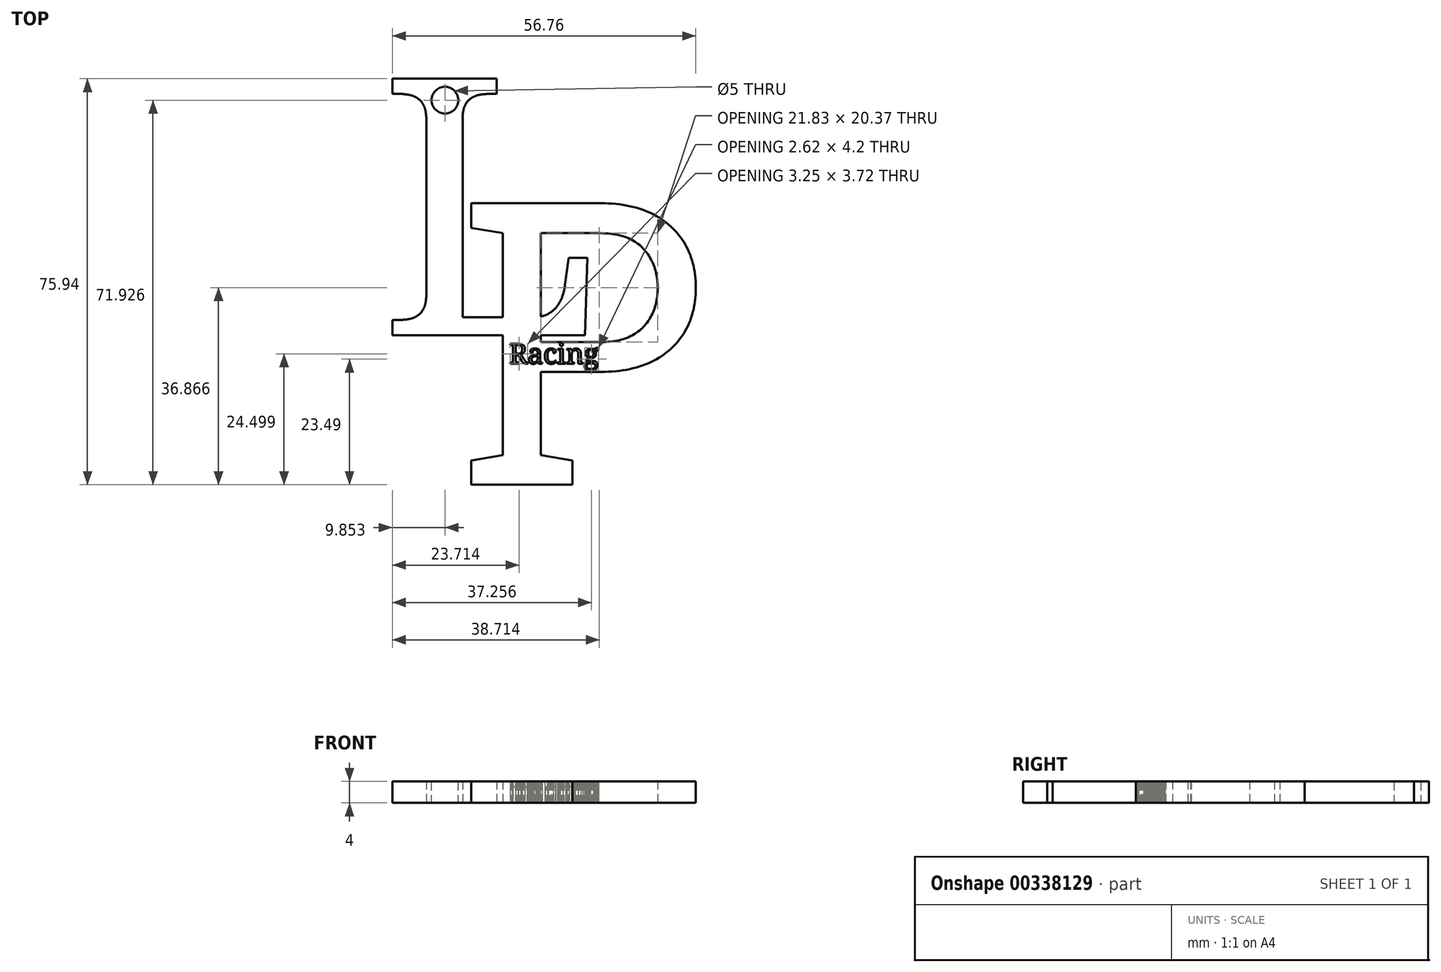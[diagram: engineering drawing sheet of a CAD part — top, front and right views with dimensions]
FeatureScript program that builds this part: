
annotation { "Feature Type Name" : "Feature", "Feature Type Description" : "" }
export const myFeature = defineFeature(function(context is Context, id is Id, definition is map)
    precondition{}
    {
        {
            var Q0;
            Q0=qCreatedBy(makeId("Top.planeOp"),FACE);
            var sketch = newSketch(context, id + "F0", { "sketchPlane" : qUnion([Q0])});
            skText(sketch, "E0", { "text": "L", "fontName": "NotoSerif-Regular.ttf"});
            skText(sketch, "E1", { "text": "P", "fontName": "RobotoSlab-Regular.ttf"});
            skText(sketch, "E2", { "text": "Racing", "fontName": "NotoSerif-Regular.ttf"});
            const initialGuessF0  = {"E0": [-0.08175, -0.00586, 1, 0, 0.04837], "E1": [-0.06698, -0.03384, 1, 0, 0.05332], "E2": [-0.0573, -0.0112, 1, 0, 0.00375]};
            skSetInitialGuess(sketch, initialGuessF0);
            skSolve(sketch);
        }
        {
            var Q0;
            Q0=makeQuery(id+"F0.imprint","IMPRINT",FACE,{"disambiguationData":[TD([[makeQuery(id+"F0.imprint","IMPRINT",EDGE,{"derivedFrom":sQuery(id+"F0.wireOp",EDGE,"E2.sketch_text.stroke-0")}),-1.0]])]});
            var Q1;
            Q1=makeQuery(id+"F0.imprint","IMPRINT",FACE,{"disambiguationData":[TD([[makeQuery(id+"F0.imprint","IMPRINT",EDGE,{"derivedFrom":sQuery(id+"F0.wireOp",EDGE,"E2.sketch_text.stroke-51")}),-1.0]])]});
            var Q2;
            Q2=makeQuery(id+"F0.imprint","IMPRINT",FACE,{"disambiguationData":[TD([[makeQuery(id+"F0.imprint","IMPRINT",EDGE,{"derivedFrom":sQuery(id+"F0.wireOp",EDGE,"E2.sketch_text.stroke-103")}),-1.0]])]});
            var Q3;
            Q3=makeQuery(id+"F0.imprint","IMPRINT",FACE,{"disambiguationData":[TD([[makeQuery(id+"F0.imprint","IMPRINT",EDGE,{"derivedFrom":sQuery(id+"F0.wireOp",EDGE,"E2.sketch_text.stroke-135")}),-1.0]])]});
            var Q4;
            Q4=makeQuery(id+"F0.imprint","IMPRINT",FACE,{"disambiguationData":[TD([[makeQuery(id+"F0.imprint","IMPRINT",EDGE,{"derivedFrom":sQuery(id+"F0.wireOp",EDGE,"E2.sketch_text.stroke-157")}),-1.0]])]});
            var Q5;
            Q5=makeQuery(id+"F0.imprint","IMPRINT",FACE,{"disambiguationData":[TD([[makeQuery(id+"F0.imprint","IMPRINT",EDGE,{"derivedFrom":sQuery(id+"F0.wireOp",EDGE,"E2.sketch_text.stroke-173")}),-1.0]])]});
            var Q6;
            Q6=makeQuery(id+"F0.imprint","IMPRINT",FACE,{"disambiguationData":[TD([[makeQuery(id+"F0.imprint","IMPRINT",EDGE,{"derivedFrom":sQuery(id+"F0.wireOp",EDGE,"E2.sketch_text.stroke-222")}),-1.0]])]});
            extrude(context, id + "F1", {"entities" : qUnion([Q0, Q1, Q2, Q3, Q4, Q5, Q6]), "depth" : 3 * mm});
        }
        {
            var Q0;
            Q0=makeQuery(id+"F0.imprint","IMPRINT",FACE,{"disambiguationData":[TD([[makeQuery(id+"F0.imprint","IMPRINT",EDGE,{"derivedFrom":sQuery(id+"F0.wireOp",EDGE,"E2.sketch_text.stroke-40")}),1.0]])]});
            var Q1;
            Q1=makeQuery(id+"F0.imprint","IMPRINT",FACE,{"disambiguationData":[TD([[makeQuery(id+"F0.imprint","IMPRINT",EDGE,{"derivedFrom":sQuery(id+"F0.wireOp",EDGE,"E2.sketch_text.stroke-51")}),1.0]])]});
            var Q2;
            Q2=makeQuery(id+"F0.imprint","IMPRINT",FACE,{"disambiguationData":[TD([[makeQuery(id+"F0.imprint","IMPRINT",EDGE,{"derivedFrom":sQuery(id+"F0.wireOp",EDGE,"E2.sketch_text.stroke-308")}),1.0]])]});
            var Q3;
            Q3=makeQuery(id+"F0.imprint","IMPRINT",FACE,{"disambiguationData":[TD([[makeQuery(id+"F0.imprint","IMPRINT",EDGE,{"derivedFrom":sQuery(id+"F0.wireOp",EDGE,"E2.sketch_text.stroke-291")}),1.0]])]});
            var Q4;
            Q4=makeQuery(id+"F0.imprint","IMPRINT",FACE,{"disambiguationData":[TD([[makeQuery(id+"F0.imprint","IMPRINT",EDGE,{"derivedFrom":sQuery(id+"F0.wireOp",EDGE,"E1.sketch_text.stroke-0")}),-1.0]])]});
            var Q5;
            {var subQ5=sQuery(id+"F0.wireOp",EDGE,"E0.sketch_text.stroke-23");Q5=makeQuery(id+"F0.imprint","IMPRINT",FACE,{"disambiguationData":[TD([[makeQuery(id+"F0.imprint","IMPRINT",EDGE,{"derivedFrom":subQ5}),-1.0]])]});}
            var Q6;
            {var subQ4=sQuery(id+"F0.wireOp",EDGE,"E0.sketch_text.stroke-0");Q6=makeQuery(id+"F0.imprint","IMPRINT",FACE,{"disambiguationData":[TD([[makeQuery(id+"F0.imprint","IMPRINT",EDGE,{"derivedFrom":subQ4}),-1.0]])]});}
            var Q7;
            {var subQ1=sQuery(id+"F0.wireOp",EDGE,"E0.sketch_text.stroke-21");var subQ5=sQuery(id+"F0.wireOp",EDGE,"E0.sketch_text.stroke-22");var subQ6=makeQuery(id+"F0.imprint","INTERSECT",VERTEX,{"derivedFrom":[subQ1,subQ5]});Q7=makeQuery(id+"F0.imprint","IMPRINT",FACE,{"disambiguationData":[TD([[makeQuery(id+"F0.imprint","IMPRINT",EDGE,{"disambiguationData":[TD([[subQ6,1.0]])],"derivedFrom":subQ1}),-1.0]])]});}
            extrude(context, id + "F2", {"entities" : qUnion([Q0, Q1, Q2, Q3, Q4, Q5, Q6, Q7]), "depth" : 4 * mm});
        }
        {
            var Q0;
            Q0=makeQuery(id+"F2.opExtrude","CAP_FACE",FACE,{"disambiguationData":[OSD([sQuery(id+"F0.wireOp",EDGE,"E0.sketch_text.stroke-0"),sQuery(id+"F0.wireOp",EDGE,"E0.sketch_text.stroke-1"),sQuery(id+"F0.wireOp",EDGE,"E0.sketch_text.stroke-2"),sQuery(id+"F0.wireOp",EDGE,"E0.sketch_text.stroke-3"),sQuery(id+"F0.wireOp",EDGE,"E0.sketch_text.stroke-4"),sQuery(id+"F0.wireOp",EDGE,"E0.sketch_text.stroke-5"),sQuery(id+"F0.wireOp",EDGE,"E0.sketch_text.stroke-6"),sQuery(id+"F0.wireOp",EDGE,"E0.sketch_text.stroke-7"),sQuery(id+"F0.wireOp",EDGE,"E0.sketch_text.stroke-8"),sQuery(id+"F0.wireOp",EDGE,"E0.sketch_text.stroke-9"),sQuery(id+"F0.wireOp",EDGE,"E0.sketch_text.stroke-10"),sQuery(id+"F0.wireOp",EDGE,"E0.sketch_text.stroke-11"),sQuery(id+"F0.wireOp",EDGE,"E0.sketch_text.stroke-12"),sQuery(id+"F0.wireOp",EDGE,"E0.sketch_text.stroke-13"),sQuery(id+"F0.wireOp",EDGE,"E0.sketch_text.stroke-14"),sQuery(id+"F0.wireOp",EDGE,"E0.sketch_text.stroke-15"),sQuery(id+"F0.wireOp",EDGE,"E0.sketch_text.stroke-16"),sQuery(id+"F0.wireOp",EDGE,"E0.sketch_text.stroke-17"),sQuery(id+"F0.wireOp",EDGE,"E0.sketch_text.stroke-18"),sQuery(id+"F0.wireOp",EDGE,"E0.sketch_text.stroke-19"),sQuery(id+"F0.wireOp",EDGE,"E0.sketch_text.stroke-20"),sQuery(id+"F0.wireOp",EDGE,"E0.sketch_text.stroke-21"),sQuery(id+"F0.wireOp",EDGE,"E0.sketch_text.stroke-22"),sQuery(id+"F0.wireOp",EDGE,"E0.sketch_text.stroke-23"),sQuery(id+"F0.wireOp",EDGE,"E0.sketch_text.stroke-24"),sQuery(id+"F0.wireOp",EDGE,"E0.sketch_text.stroke-25"),sQuery(id+"F0.wireOp",EDGE,"E0.sketch_text.stroke-26"),sQuery(id+"F0.wireOp",EDGE,"E0.sketch_text.stroke-27"),sQuery(id+"F0.wireOp",EDGE,"E0.sketch_text.stroke-28"),sQuery(id+"F0.wireOp",EDGE,"E0.sketch_text.stroke-29"),sQuery(id+"F0.wireOp",EDGE,"E1.sketch_text.stroke-0"),sQuery(id+"F0.wireOp",EDGE,"E1.sketch_text.stroke-1"),sQuery(id+"F0.wireOp",EDGE,"E1.sketch_text.stroke-2"),sQuery(id+"F0.wireOp",EDGE,"E1.sketch_text.stroke-3"),sQuery(id+"F0.wireOp",EDGE,"E1.sketch_text.stroke-4"),sQuery(id+"F0.wireOp",EDGE,"E1.sketch_text.stroke-5"),sQuery(id+"F0.wireOp",EDGE,"E1.sketch_text.stroke-6"),sQuery(id+"F0.wireOp",EDGE,"E1.sketch_text.stroke-7"),sQuery(id+"F0.wireOp",EDGE,"E1.sketch_text.stroke-8"),sQuery(id+"F0.wireOp",EDGE,"E1.sketch_text.stroke-9"),sQuery(id+"F0.wireOp",EDGE,"E1.sketch_text.stroke-10"),sQuery(id+"F0.wireOp",EDGE,"E1.sketch_text.stroke-11"),sQuery(id+"F0.wireOp",EDGE,"E1.sketch_text.stroke-12"),sQuery(id+"F0.wireOp",EDGE,"E1.sketch_text.stroke-13"),sQuery(id+"F0.wireOp",EDGE,"E1.sketch_text.stroke-14"),sQuery(id+"F0.wireOp",EDGE,"E1.sketch_text.stroke-15"),sQuery(id+"F0.wireOp",EDGE,"E1.sketch_text.stroke-16"),sQuery(id+"F0.wireOp",EDGE,"E1.sketch_text.stroke-17"),sQuery(id+"F0.wireOp",EDGE,"E1.sketch_text.stroke-18"),sQuery(id+"F0.wireOp",EDGE,"E1.sketch_text.stroke-19"),sQuery(id+"F0.wireOp",EDGE,"E1.sketch_text.stroke-20"),sQuery(id+"F0.wireOp",EDGE,"E1.sketch_text.stroke-21"),sQuery(id+"F0.wireOp",EDGE,"E1.sketch_text.stroke-22"),sQuery(id+"F0.wireOp",EDGE,"E2.sketch_text.stroke-0"),sQuery(id+"F0.wireOp",EDGE,"E2.sketch_text.stroke-1"),sQuery(id+"F0.wireOp",EDGE,"E2.sketch_text.stroke-2"),sQuery(id+"F0.wireOp",EDGE,"E2.sketch_text.stroke-3"),sQuery(id+"F0.wireOp",EDGE,"E2.sketch_text.stroke-4"),sQuery(id+"F0.wireOp",EDGE,"E2.sketch_text.stroke-5"),sQuery(id+"F0.wireOp",EDGE,"E2.sketch_text.stroke-6"),sQuery(id+"F0.wireOp",EDGE,"E2.sketch_text.stroke-7"),sQuery(id+"F0.wireOp",EDGE,"E2.sketch_text.stroke-8"),sQuery(id+"F0.wireOp",EDGE,"E2.sketch_text.stroke-9"),sQuery(id+"F0.wireOp",EDGE,"E2.sketch_text.stroke-10"),sQuery(id+"F0.wireOp",EDGE,"E2.sketch_text.stroke-11"),sQuery(id+"F0.wireOp",EDGE,"E2.sketch_text.stroke-12"),sQuery(id+"F0.wireOp",EDGE,"E2.sketch_text.stroke-13"),sQuery(id+"F0.wireOp",EDGE,"E2.sketch_text.stroke-14"),sQuery(id+"F0.wireOp",EDGE,"E2.sketch_text.stroke-15"),sQuery(id+"F0.wireOp",EDGE,"E2.sketch_text.stroke-16"),sQuery(id+"F0.wireOp",EDGE,"E2.sketch_text.stroke-17"),sQuery(id+"F0.wireOp",EDGE,"E2.sketch_text.stroke-18"),sQuery(id+"F0.wireOp",EDGE,"E2.sketch_text.stroke-19"),sQuery(id+"F0.wireOp",EDGE,"E2.sketch_text.stroke-20"),sQuery(id+"F0.wireOp",EDGE,"E2.sketch_text.stroke-21"),sQuery(id+"F0.wireOp",EDGE,"E2.sketch_text.stroke-22"),sQuery(id+"F0.wireOp",EDGE,"E2.sketch_text.stroke-23"),sQuery(id+"F0.wireOp",EDGE,"E2.sketch_text.stroke-24"),sQuery(id+"F0.wireOp",EDGE,"E2.sketch_text.stroke-25"),sQuery(id+"F0.wireOp",EDGE,"E2.sketch_text.stroke-26"),sQuery(id+"F0.wireOp",EDGE,"E2.sketch_text.stroke-27"),sQuery(id+"F0.wireOp",EDGE,"E2.sketch_text.stroke-28"),sQuery(id+"F0.wireOp",EDGE,"E2.sketch_text.stroke-29"),sQuery(id+"F0.wireOp",EDGE,"E2.sketch_text.stroke-30"),sQuery(id+"F0.wireOp",EDGE,"E2.sketch_text.stroke-31"),sQuery(id+"F0.wireOp",EDGE,"E2.sketch_text.stroke-32"),sQuery(id+"F0.wireOp",EDGE,"E2.sketch_text.stroke-33"),sQuery(id+"F0.wireOp",EDGE,"E2.sketch_text.stroke-34"),sQuery(id+"F0.wireOp",EDGE,"E2.sketch_text.stroke-35"),sQuery(id+"F0.wireOp",EDGE,"E2.sketch_text.stroke-36"),sQuery(id+"F0.wireOp",EDGE,"E2.sketch_text.stroke-37"),sQuery(id+"F0.wireOp",EDGE,"E2.sketch_text.stroke-38"),sQuery(id+"F0.wireOp",EDGE,"E2.sketch_text.stroke-39"),sQuery(id+"F0.wireOp",EDGE,"E2.sketch_text.stroke-63"),sQuery(id+"F0.wireOp",EDGE,"E2.sketch_text.stroke-64"),sQuery(id+"F0.wireOp",EDGE,"E2.sketch_text.stroke-65"),sQuery(id+"F0.wireOp",EDGE,"E2.sketch_text.stroke-66"),sQuery(id+"F0.wireOp",EDGE,"E2.sketch_text.stroke-67"),sQuery(id+"F0.wireOp",EDGE,"E2.sketch_text.stroke-68"),sQuery(id+"F0.wireOp",EDGE,"E2.sketch_text.stroke-69"),sQuery(id+"F0.wireOp",EDGE,"E2.sketch_text.stroke-70"),sQuery(id+"F0.wireOp",EDGE,"E2.sketch_text.stroke-71"),sQuery(id+"F0.wireOp",EDGE,"E2.sketch_text.stroke-72"),sQuery(id+"F0.wireOp",EDGE,"E2.sketch_text.stroke-73"),sQuery(id+"F0.wireOp",EDGE,"E2.sketch_text.stroke-74"),sQuery(id+"F0.wireOp",EDGE,"E2.sketch_text.stroke-75"),sQuery(id+"F0.wireOp",EDGE,"E2.sketch_text.stroke-76"),sQuery(id+"F0.wireOp",EDGE,"E2.sketch_text.stroke-77"),sQuery(id+"F0.wireOp",EDGE,"E2.sketch_text.stroke-78"),sQuery(id+"F0.wireOp",EDGE,"E2.sketch_text.stroke-79"),sQuery(id+"F0.wireOp",EDGE,"E2.sketch_text.stroke-80"),sQuery(id+"F0.wireOp",EDGE,"E2.sketch_text.stroke-81"),sQuery(id+"F0.wireOp",EDGE,"E2.sketch_text.stroke-82"),sQuery(id+"F0.wireOp",EDGE,"E2.sketch_text.stroke-83"),sQuery(id+"F0.wireOp",EDGE,"E2.sketch_text.stroke-84"),sQuery(id+"F0.wireOp",EDGE,"E2.sketch_text.stroke-85"),sQuery(id+"F0.wireOp",EDGE,"E2.sketch_text.stroke-86"),sQuery(id+"F0.wireOp",EDGE,"E2.sketch_text.stroke-87"),sQuery(id+"F0.wireOp",EDGE,"E2.sketch_text.stroke-88"),sQuery(id+"F0.wireOp",EDGE,"E2.sketch_text.stroke-89"),sQuery(id+"F0.wireOp",EDGE,"E2.sketch_text.stroke-90"),sQuery(id+"F0.wireOp",EDGE,"E2.sketch_text.stroke-91"),sQuery(id+"F0.wireOp",EDGE,"E2.sketch_text.stroke-92"),sQuery(id+"F0.wireOp",EDGE,"E2.sketch_text.stroke-93"),sQuery(id+"F0.wireOp",EDGE,"E2.sketch_text.stroke-94"),sQuery(id+"F0.wireOp",EDGE,"E2.sketch_text.stroke-95"),sQuery(id+"F0.wireOp",EDGE,"E2.sketch_text.stroke-96"),sQuery(id+"F0.wireOp",EDGE,"E2.sketch_text.stroke-97"),sQuery(id+"F0.wireOp",EDGE,"E2.sketch_text.stroke-98"),sQuery(id+"F0.wireOp",EDGE,"E2.sketch_text.stroke-99"),sQuery(id+"F0.wireOp",EDGE,"E2.sketch_text.stroke-100"),sQuery(id+"F0.wireOp",EDGE,"E2.sketch_text.stroke-101"),sQuery(id+"F0.wireOp",EDGE,"E2.sketch_text.stroke-102"),sQuery(id+"F0.wireOp",EDGE,"E2.sketch_text.stroke-103"),sQuery(id+"F0.wireOp",EDGE,"E2.sketch_text.stroke-104"),sQuery(id+"F0.wireOp",EDGE,"E2.sketch_text.stroke-105"),sQuery(id+"F0.wireOp",EDGE,"E2.sketch_text.stroke-106"),sQuery(id+"F0.wireOp",EDGE,"E2.sketch_text.stroke-107"),sQuery(id+"F0.wireOp",EDGE,"E2.sketch_text.stroke-108"),sQuery(id+"F0.wireOp",EDGE,"E2.sketch_text.stroke-109"),sQuery(id+"F0.wireOp",EDGE,"E2.sketch_text.stroke-110"),sQuery(id+"F0.wireOp",EDGE,"E2.sketch_text.stroke-111"),sQuery(id+"F0.wireOp",EDGE,"E2.sketch_text.stroke-112"),sQuery(id+"F0.wireOp",EDGE,"E2.sketch_text.stroke-113"),sQuery(id+"F0.wireOp",EDGE,"E2.sketch_text.stroke-114"),sQuery(id+"F0.wireOp",EDGE,"E2.sketch_text.stroke-115"),sQuery(id+"F0.wireOp",EDGE,"E2.sketch_text.stroke-116"),sQuery(id+"F0.wireOp",EDGE,"E2.sketch_text.stroke-117"),sQuery(id+"F0.wireOp",EDGE,"E2.sketch_text.stroke-118"),sQuery(id+"F0.wireOp",EDGE,"E2.sketch_text.stroke-119"),sQuery(id+"F0.wireOp",EDGE,"E2.sketch_text.stroke-120"),sQuery(id+"F0.wireOp",EDGE,"E2.sketch_text.stroke-121"),sQuery(id+"F0.wireOp",EDGE,"E2.sketch_text.stroke-122"),sQuery(id+"F0.wireOp",EDGE,"E2.sketch_text.stroke-123"),sQuery(id+"F0.wireOp",EDGE,"E2.sketch_text.stroke-124"),sQuery(id+"F0.wireOp",EDGE,"E2.sketch_text.stroke-125"),sQuery(id+"F0.wireOp",EDGE,"E2.sketch_text.stroke-126"),sQuery(id+"F0.wireOp",EDGE,"E2.sketch_text.stroke-127"),sQuery(id+"F0.wireOp",EDGE,"E2.sketch_text.stroke-128"),sQuery(id+"F0.wireOp",EDGE,"E2.sketch_text.stroke-129"),sQuery(id+"F0.wireOp",EDGE,"E2.sketch_text.stroke-130"),sQuery(id+"F0.wireOp",EDGE,"E2.sketch_text.stroke-131"),sQuery(id+"F0.wireOp",EDGE,"E2.sketch_text.stroke-132"),sQuery(id+"F0.wireOp",EDGE,"E2.sketch_text.stroke-133"),sQuery(id+"F0.wireOp",EDGE,"E2.sketch_text.stroke-134"),sQuery(id+"F0.wireOp",EDGE,"E2.sketch_text.stroke-135"),sQuery(id+"F0.wireOp",EDGE,"E2.sketch_text.stroke-136"),sQuery(id+"F0.wireOp",EDGE,"E2.sketch_text.stroke-137"),sQuery(id+"F0.wireOp",EDGE,"E2.sketch_text.stroke-138"),sQuery(id+"F0.wireOp",EDGE,"E2.sketch_text.stroke-139"),sQuery(id+"F0.wireOp",EDGE,"E2.sketch_text.stroke-140"),sQuery(id+"F0.wireOp",EDGE,"E2.sketch_text.stroke-141"),sQuery(id+"F0.wireOp",EDGE,"E2.sketch_text.stroke-142"),sQuery(id+"F0.wireOp",EDGE,"E2.sketch_text.stroke-143"),sQuery(id+"F0.wireOp",EDGE,"E2.sketch_text.stroke-144"),sQuery(id+"F0.wireOp",EDGE,"E2.sketch_text.stroke-145"),sQuery(id+"F0.wireOp",EDGE,"E2.sketch_text.stroke-146"),sQuery(id+"F0.wireOp",EDGE,"E2.sketch_text.stroke-147"),sQuery(id+"F0.wireOp",EDGE,"E2.sketch_text.stroke-148"),sQuery(id+"F0.wireOp",EDGE,"E2.sketch_text.stroke-149"),sQuery(id+"F0.wireOp",EDGE,"E2.sketch_text.stroke-150"),sQuery(id+"F0.wireOp",EDGE,"E2.sketch_text.stroke-151"),sQuery(id+"F0.wireOp",EDGE,"E2.sketch_text.stroke-152"),sQuery(id+"F0.wireOp",EDGE,"E2.sketch_text.stroke-153"),sQuery(id+"F0.wireOp",EDGE,"E2.sketch_text.stroke-154"),sQuery(id+"F0.wireOp",EDGE,"E2.sketch_text.stroke-155"),sQuery(id+"F0.wireOp",EDGE,"E2.sketch_text.stroke-156"),sQuery(id+"F0.wireOp",EDGE,"E2.sketch_text.stroke-157"),sQuery(id+"F0.wireOp",EDGE,"E2.sketch_text.stroke-158"),sQuery(id+"F0.wireOp",EDGE,"E2.sketch_text.stroke-159"),sQuery(id+"F0.wireOp",EDGE,"E2.sketch_text.stroke-160"),sQuery(id+"F0.wireOp",EDGE,"E2.sketch_text.stroke-161"),sQuery(id+"F0.wireOp",EDGE,"E2.sketch_text.stroke-162"),sQuery(id+"F0.wireOp",EDGE,"E2.sketch_text.stroke-163"),sQuery(id+"F0.wireOp",EDGE,"E2.sketch_text.stroke-164"),sQuery(id+"F0.wireOp",EDGE,"E2.sketch_text.stroke-165"),sQuery(id+"F0.wireOp",EDGE,"E2.sketch_text.stroke-166"),sQuery(id+"F0.wireOp",EDGE,"E2.sketch_text.stroke-167"),sQuery(id+"F0.wireOp",EDGE,"E2.sketch_text.stroke-168"),sQuery(id+"F0.wireOp",EDGE,"E2.sketch_text.stroke-169"),sQuery(id+"F0.wireOp",EDGE,"E2.sketch_text.stroke-170"),sQuery(id+"F0.wireOp",EDGE,"E2.sketch_text.stroke-171"),sQuery(id+"F0.wireOp",EDGE,"E2.sketch_text.stroke-172"),sQuery(id+"F0.wireOp",EDGE,"E2.sketch_text.stroke-173"),sQuery(id+"F0.wireOp",EDGE,"E2.sketch_text.stroke-174"),sQuery(id+"F0.wireOp",EDGE,"E2.sketch_text.stroke-175"),sQuery(id+"F0.wireOp",EDGE,"E2.sketch_text.stroke-176"),sQuery(id+"F0.wireOp",EDGE,"E2.sketch_text.stroke-177"),sQuery(id+"F0.wireOp",EDGE,"E2.sketch_text.stroke-178"),sQuery(id+"F0.wireOp",EDGE,"E2.sketch_text.stroke-179"),sQuery(id+"F0.wireOp",EDGE,"E2.sketch_text.stroke-180"),sQuery(id+"F0.wireOp",EDGE,"E2.sketch_text.stroke-181"),sQuery(id+"F0.wireOp",EDGE,"E2.sketch_text.stroke-182"),sQuery(id+"F0.wireOp",EDGE,"E2.sketch_text.stroke-183"),sQuery(id+"F0.wireOp",EDGE,"E2.sketch_text.stroke-184"),sQuery(id+"F0.wireOp",EDGE,"E2.sketch_text.stroke-185"),sQuery(id+"F0.wireOp",EDGE,"E2.sketch_text.stroke-186"),sQuery(id+"F0.wireOp",EDGE,"E2.sketch_text.stroke-187"),sQuery(id+"F0.wireOp",EDGE,"E2.sketch_text.stroke-188"),sQuery(id+"F0.wireOp",EDGE,"E2.sketch_text.stroke-189"),sQuery(id+"F0.wireOp",EDGE,"E2.sketch_text.stroke-190"),sQuery(id+"F0.wireOp",EDGE,"E2.sketch_text.stroke-191"),sQuery(id+"F0.wireOp",EDGE,"E2.sketch_text.stroke-192"),sQuery(id+"F0.wireOp",EDGE,"E2.sketch_text.stroke-193"),sQuery(id+"F0.wireOp",EDGE,"E2.sketch_text.stroke-194"),sQuery(id+"F0.wireOp",EDGE,"E2.sketch_text.stroke-195"),sQuery(id+"F0.wireOp",EDGE,"E2.sketch_text.stroke-196"),sQuery(id+"F0.wireOp",EDGE,"E2.sketch_text.stroke-197"),sQuery(id+"F0.wireOp",EDGE,"E2.sketch_text.stroke-198"),sQuery(id+"F0.wireOp",EDGE,"E2.sketch_text.stroke-199"),sQuery(id+"F0.wireOp",EDGE,"E2.sketch_text.stroke-200"),sQuery(id+"F0.wireOp",EDGE,"E2.sketch_text.stroke-201"),sQuery(id+"F0.wireOp",EDGE,"E2.sketch_text.stroke-202"),sQuery(id+"F0.wireOp",EDGE,"E2.sketch_text.stroke-203"),sQuery(id+"F0.wireOp",EDGE,"E2.sketch_text.stroke-204"),sQuery(id+"F0.wireOp",EDGE,"E2.sketch_text.stroke-205"),sQuery(id+"F0.wireOp",EDGE,"E2.sketch_text.stroke-206"),sQuery(id+"F0.wireOp",EDGE,"E2.sketch_text.stroke-207"),sQuery(id+"F0.wireOp",EDGE,"E2.sketch_text.stroke-208"),sQuery(id+"F0.wireOp",EDGE,"E2.sketch_text.stroke-209"),sQuery(id+"F0.wireOp",EDGE,"E2.sketch_text.stroke-210"),sQuery(id+"F0.wireOp",EDGE,"E2.sketch_text.stroke-211"),sQuery(id+"F0.wireOp",EDGE,"E2.sketch_text.stroke-212"),sQuery(id+"F0.wireOp",EDGE,"E2.sketch_text.stroke-213"),sQuery(id+"F0.wireOp",EDGE,"E2.sketch_text.stroke-214"),sQuery(id+"F0.wireOp",EDGE,"E2.sketch_text.stroke-215"),sQuery(id+"F0.wireOp",EDGE,"E2.sketch_text.stroke-216"),sQuery(id+"F0.wireOp",EDGE,"E2.sketch_text.stroke-217"),sQuery(id+"F0.wireOp",EDGE,"E2.sketch_text.stroke-218"),sQuery(id+"F0.wireOp",EDGE,"E2.sketch_text.stroke-219"),sQuery(id+"F0.wireOp",EDGE,"E2.sketch_text.stroke-220"),sQuery(id+"F0.wireOp",EDGE,"E2.sketch_text.stroke-221"),sQuery(id+"F0.wireOp",EDGE,"E2.sketch_text.stroke-222"),sQuery(id+"F0.wireOp",EDGE,"E2.sketch_text.stroke-223"),sQuery(id+"F0.wireOp",EDGE,"E2.sketch_text.stroke-224"),sQuery(id+"F0.wireOp",EDGE,"E2.sketch_text.stroke-225"),sQuery(id+"F0.wireOp",EDGE,"E2.sketch_text.stroke-226"),sQuery(id+"F0.wireOp",EDGE,"E2.sketch_text.stroke-227"),sQuery(id+"F0.wireOp",EDGE,"E2.sketch_text.stroke-228"),sQuery(id+"F0.wireOp",EDGE,"E2.sketch_text.stroke-229"),sQuery(id+"F0.wireOp",EDGE,"E2.sketch_text.stroke-230"),sQuery(id+"F0.wireOp",EDGE,"E2.sketch_text.stroke-231"),sQuery(id+"F0.wireOp",EDGE,"E2.sketch_text.stroke-232"),sQuery(id+"F0.wireOp",EDGE,"E2.sketch_text.stroke-233"),sQuery(id+"F0.wireOp",EDGE,"E2.sketch_text.stroke-234"),sQuery(id+"F0.wireOp",EDGE,"E2.sketch_text.stroke-235"),sQuery(id+"F0.wireOp",EDGE,"E2.sketch_text.stroke-236"),sQuery(id+"F0.wireOp",EDGE,"E2.sketch_text.stroke-237"),sQuery(id+"F0.wireOp",EDGE,"E2.sketch_text.stroke-238"),sQuery(id+"F0.wireOp",EDGE,"E2.sketch_text.stroke-239"),sQuery(id+"F0.wireOp",EDGE,"E2.sketch_text.stroke-240"),sQuery(id+"F0.wireOp",EDGE,"E2.sketch_text.stroke-241"),sQuery(id+"F0.wireOp",EDGE,"E2.sketch_text.stroke-242"),sQuery(id+"F0.wireOp",EDGE,"E2.sketch_text.stroke-243"),sQuery(id+"F0.wireOp",EDGE,"E2.sketch_text.stroke-244"),sQuery(id+"F0.wireOp",EDGE,"E2.sketch_text.stroke-245"),sQuery(id+"F0.wireOp",EDGE,"E2.sketch_text.stroke-246"),sQuery(id+"F0.wireOp",EDGE,"E2.sketch_text.stroke-247"),sQuery(id+"F0.wireOp",EDGE,"E2.sketch_text.stroke-248"),sQuery(id+"F0.wireOp",EDGE,"E2.sketch_text.stroke-249"),sQuery(id+"F0.wireOp",EDGE,"E2.sketch_text.stroke-250"),sQuery(id+"F0.wireOp",EDGE,"E2.sketch_text.stroke-251"),sQuery(id+"F0.wireOp",EDGE,"E2.sketch_text.stroke-252"),sQuery(id+"F0.wireOp",EDGE,"E2.sketch_text.stroke-253"),sQuery(id+"F0.wireOp",EDGE,"E2.sketch_text.stroke-254"),sQuery(id+"F0.wireOp",EDGE,"E2.sketch_text.stroke-255"),sQuery(id+"F0.wireOp",EDGE,"E2.sketch_text.stroke-256"),sQuery(id+"F0.wireOp",EDGE,"E2.sketch_text.stroke-257"),sQuery(id+"F0.wireOp",EDGE,"E2.sketch_text.stroke-258"),sQuery(id+"F0.wireOp",EDGE,"E2.sketch_text.stroke-259"),sQuery(id+"F0.wireOp",EDGE,"E2.sketch_text.stroke-260"),sQuery(id+"F0.wireOp",EDGE,"E2.sketch_text.stroke-261"),sQuery(id+"F0.wireOp",EDGE,"E2.sketch_text.stroke-262"),sQuery(id+"F0.wireOp",EDGE,"E2.sketch_text.stroke-263"),sQuery(id+"F0.wireOp",EDGE,"E2.sketch_text.stroke-264"),sQuery(id+"F0.wireOp",EDGE,"E2.sketch_text.stroke-265"),sQuery(id+"F0.wireOp",EDGE,"E2.sketch_text.stroke-266"),sQuery(id+"F0.wireOp",EDGE,"E2.sketch_text.stroke-267"),sQuery(id+"F0.wireOp",EDGE,"E2.sketch_text.stroke-268"),sQuery(id+"F0.wireOp",EDGE,"E2.sketch_text.stroke-269"),sQuery(id+"F0.wireOp",EDGE,"E2.sketch_text.stroke-270"),sQuery(id+"F0.wireOp",EDGE,"E2.sketch_text.stroke-271"),sQuery(id+"F0.wireOp",EDGE,"E2.sketch_text.stroke-272"),sQuery(id+"F0.wireOp",EDGE,"E2.sketch_text.stroke-273"),sQuery(id+"F0.wireOp",EDGE,"E2.sketch_text.stroke-274"),sQuery(id+"F0.wireOp",EDGE,"E2.sketch_text.stroke-275"),sQuery(id+"F0.wireOp",EDGE,"E2.sketch_text.stroke-276"),sQuery(id+"F0.wireOp",EDGE,"E2.sketch_text.stroke-277"),sQuery(id+"F0.wireOp",EDGE,"E2.sketch_text.stroke-278"),sQuery(id+"F0.wireOp",EDGE,"E2.sketch_text.stroke-279"),sQuery(id+"F0.wireOp",EDGE,"E2.sketch_text.stroke-280"),sQuery(id+"F0.wireOp",EDGE,"E2.sketch_text.stroke-281"),sQuery(id+"F0.wireOp",EDGE,"E2.sketch_text.stroke-282"),sQuery(id+"F0.wireOp",EDGE,"E2.sketch_text.stroke-283"),sQuery(id+"F0.wireOp",EDGE,"E2.sketch_text.stroke-284"),sQuery(id+"F0.wireOp",EDGE,"E2.sketch_text.stroke-285"),sQuery(id+"F0.wireOp",EDGE,"E2.sketch_text.stroke-286"),sQuery(id+"F0.wireOp",EDGE,"E2.sketch_text.stroke-287"),sQuery(id+"F0.wireOp",EDGE,"E2.sketch_text.stroke-288"),sQuery(id+"F0.wireOp",EDGE,"E2.sketch_text.stroke-289"),sQuery(id+"F0.wireOp",EDGE,"E2.sketch_text.stroke-290")])],"isStart":false});
            var sketch = newSketch(context, id + "F3", { "sketchPlane" : qUnion([Q0])});
            skCircle(sketch, "E3", {"center": v(-69.34, 38.09) * mm, "radius": 2.5 * mm});
            skSolve(sketch);
        }
        {
            var Q0;
            Q0=makeQuery(id+"F3.imprint","IMPRINT",FACE,{"disambiguationData":[TD([[makeQuery(id+"F3.imprint","IMPRINT",EDGE,{"derivedFrom":sQuery(id+"F3.wireOp",EDGE,"E3")}),1.0]])]});
            var Q1;
            Q1=sQuery(id+"F3.wireOp",EDGE,"E3");
            extrude(context, id + "F4", {"entities" : qUnion([Q0]), "operationType" : NewBodyOperationType.REMOVE, "surfaceEntities" : qUnion([Q1]), "oppositeDirection" : true, "depth" : 9.65 * mm});
        }
    });
